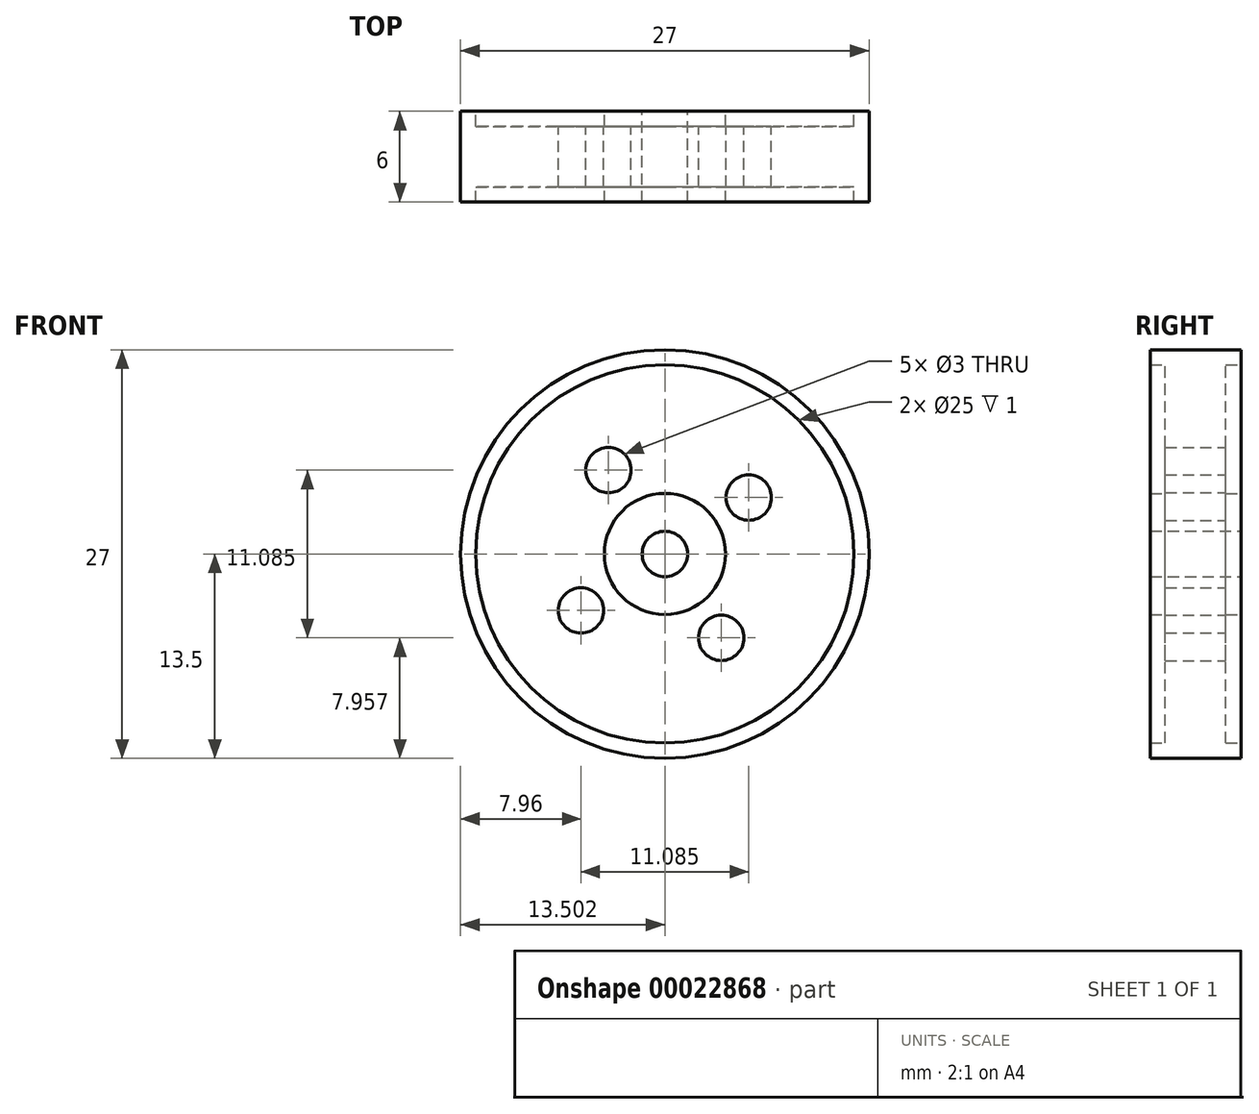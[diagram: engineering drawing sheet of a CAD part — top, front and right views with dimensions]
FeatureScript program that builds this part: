
annotation { "Feature Type Name" : "Feature", "Feature Type Description" : "" }
export const myFeature = defineFeature(function(context is Context, id is Id, definition is map)
    precondition{}
    {
        {
            var Q0;
            Q0=qCreatedBy(makeId("Front.planeOp"),FACE);
            var sketch = newSketch(context, id + "F0", { "sketchPlane" : qUnion([Q0])});
            skCircle(sketch, "E0", {"center": v(2.22, 0) * mm, "radius": 13.5 * mm});
            skCircle(sketch, "E1", {"center": v(2.22, 0) * mm, "radius": 12.5 * mm});
            skCircle(sketch, "E2", {"center": v(2.22, 0) * mm, "radius": 4 * mm});
            skCircle(sketch, "E3", {"center": v(2.22, 0) * mm, "radius": 1.5 * mm});
            skLineSegment(sketch, "E4", {"start": v(3.72, 0) * mm, "end": v(7.76, 3.73) * mm});
            skCircle(sketch, "E5", {"center": v(7.76, 3.73) * mm, "radius": 1.5 * mm});
            skCircle(sketch, "E6.1.0", {"center": v(-1.5, 5.54) * mm, "radius": 1.5 * mm});
            skCircle(sketch, "E6.2.0", {"center": v(-3.32, -3.73) * mm, "radius": 1.5 * mm});
            skCircle(sketch, "E6.3.0", {"center": v(5.95, -5.54) * mm, "radius": 1.5 * mm});
            skSolve(sketch);
        }
        {
            var Q0;
            Q0=makeQuery(id+"F0.imprint","IMPRINT",FACE,{"disambiguationData":[TD([[makeQuery(id+"F0.imprint","IMPRINT",EDGE,{"derivedFrom":sQuery(id+"F0.wireOp",EDGE,"E1")}),1.0]])]});
            extrude(context, id + "F1", {"entities" : qUnion([Q0]), "endBound" : BoundingType.SYMMETRIC, "depth" : 4 * mm});
        }
        {
            var Q0;
            Q0=makeQuery(id+"F0.imprint","IMPRINT",FACE,{"disambiguationData":[TD([[makeQuery(id+"F0.imprint","IMPRINT",EDGE,{"derivedFrom":sQuery(id+"F0.wireOp",EDGE,"E0")}),1.0]])]});
            extrude(context, id + "F2", {"entities" : qUnion([Q0]), "operationType" : NewBodyOperationType.ADD, "endBound" : BoundingType.SYMMETRIC, "depth" : 6 * mm});
        }
        {
            var Q0;
            Q0=makeQuery(id+"F0.imprint","IMPRINT",FACE,{"disambiguationData":[TD([[makeQuery(id+"F0.imprint","IMPRINT",EDGE,{"derivedFrom":sQuery(id+"F0.wireOp",EDGE,"E2")}),1.0]])]});
            extrude(context, id + "F3", {"entities" : qUnion([Q0]), "operationType" : NewBodyOperationType.ADD, "endBound" : BoundingType.SYMMETRIC, "depth" : 6 * mm});
        }
    });
